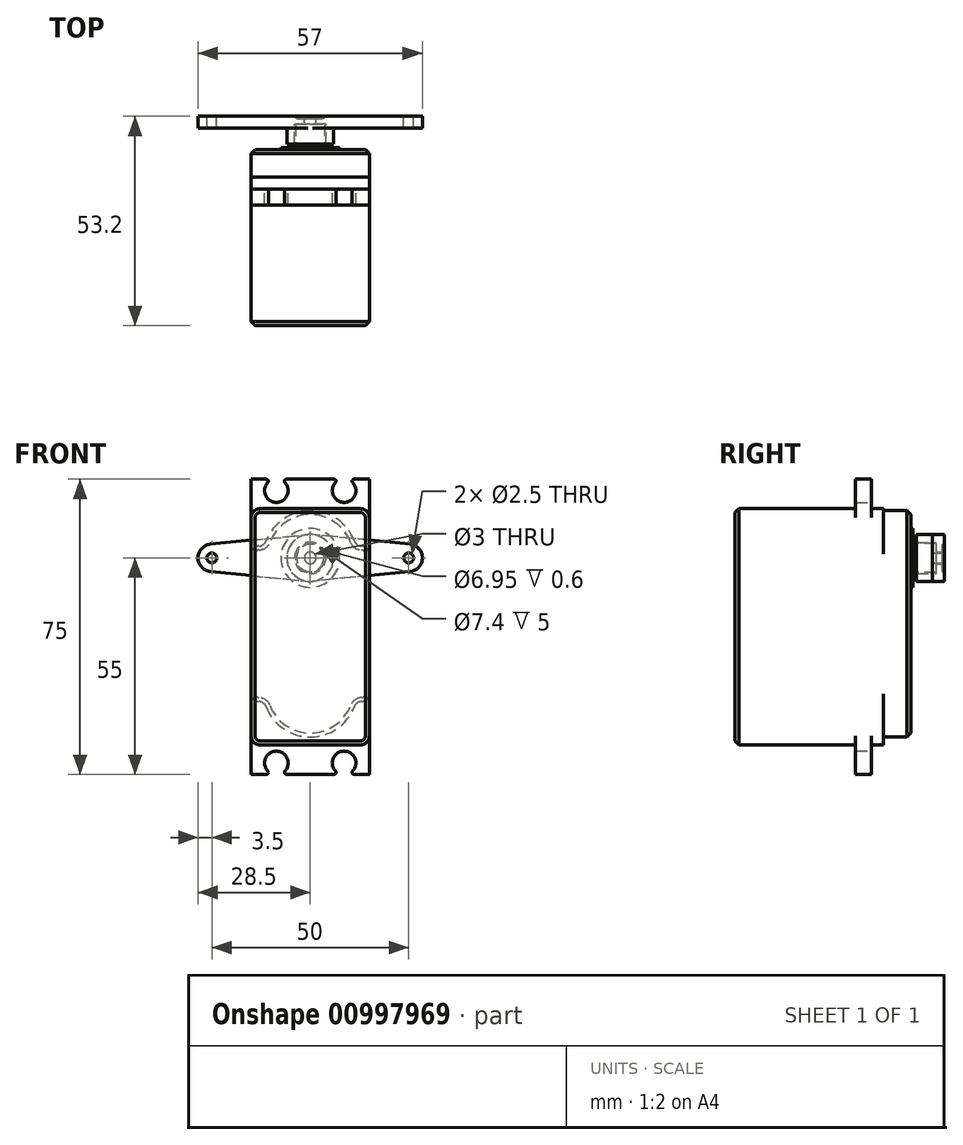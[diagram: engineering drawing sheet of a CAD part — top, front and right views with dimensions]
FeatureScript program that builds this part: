
annotation { "Feature Type Name" : "Feature", "Feature Type Description" : "" }
export const myFeature = defineFeature(function(context is Context, id is Id, definition is map)
    precondition{}
    {
        {
            var Q0;
            Q0=qCreatedBy(makeId("Front.planeOp"),FACE);
            var sketch = newSketch(context, id + "F0", { "sketchPlane" : qUnion([Q0])});
            skArc(sketch, "E0", {"start": v(-0.58, -5.92) * mm, "mid": v(0, -5.95) * mm, "end": v(0.58, -5.92) * mm});
            skCircle(sketch, "E1", {"center": v(0, 0) * mm, "radius": 28.5 * mm, "construction": true});
            skArc(sketch, "E2", {"start": v(-25.34, 3.48) * mm, "mid": v(-28.5, 0) * mm, "end": v(-25.34, -3.48) * mm});
            skArc(sketch, "E3.MirrorC", {"start": v(25.34, 3.48) * mm, "mid": v(28.5, 0) * mm, "end": v(25.34, -3.48) * mm});
            skLineSegment(sketch, "E4", {"start": v(-25.34, 3.48) * mm, "end": v(-0.58, 5.92) * mm});
            skLineSegment(sketch, "E5.MirrorCS", {"start": v(-25.34, -3.48) * mm, "end": v(-0.58, -5.92) * mm});
            skLineSegment(sketch, "E6.MirrorCS", {"start": v(25.34, 3.48) * mm, "end": v(0.58, 5.92) * mm});
            skLineSegment(sketch, "E7.MirrorCS", {"start": v(25.34, -3.48) * mm, "end": v(0.58, -5.92) * mm});
            skPoint(sketch, "E8.orphan", {"position": v(-30.14, 3.01) * mm});
            skPoint(sketch, "E9.orphan", {"position": v(-30.14, -3.01) * mm});
            skPoint(sketch, "E10.orphan", {"position": v(-3.18, 6.3) * mm});
            skPoint(sketch, "E11.orphan", {"position": v(3.18, 6.3) * mm});
            skPoint(sketch, "E12.orphan", {"position": v(-3.18, -6.3) * mm});
            skPoint(sketch, "E13.orphan", {"position": v(3.18, -6.3) * mm});
            skArc(sketch, "E14.trimOffspring", {"start": v(0.58, 5.92) * mm, "mid": v(0, 5.95) * mm, "end": v(-0.58, 5.92) * mm});
            skPoint(sketch, "E15.orphan", {"position": v(30.14, 3.01) * mm});
            skPoint(sketch, "E16.orphan", {"position": v(30.14, -3.01) * mm});
            skCircle(sketch, "E17", {"center": v(-25, 0) * mm, "radius": 1.25 * mm});
            skCircle(sketch, "E18.MirrorC", {"center": v(25, 0) * mm, "radius": 1.25 * mm});
            skSolve(sketch);
        }
        {
            var Q0;
            Q0=makeQuery(id+"F0.imprint","IMPRINT",FACE,{"disambiguationData":[TD([[makeQuery(id+"F0.imprint","IMPRINT",EDGE,{"derivedFrom":sQuery(id+"F0.wireOp",EDGE,"E0")}),1.0]])]});
            extrude(context, id + "F1", {"entities" : qUnion([Q0]), "depth" : 3 * mm, "offsetDistance" : 25 * mm});
        }
        {
            var Q0;
            Q0=makeQuery(id+"F1.opExtrude","CAP_FACE",FACE,{"disambiguationData":[OSD([sQuery(id+"F0.wireOp",EDGE,"E0"),sQuery(id+"F0.wireOp",EDGE,"E2"),sQuery(id+"F0.wireOp",EDGE,"E3.MirrorC"),sQuery(id+"F0.wireOp",EDGE,"E4"),sQuery(id+"F0.wireOp",EDGE,"E5.MirrorCS"),sQuery(id+"F0.wireOp",EDGE,"E6.MirrorCS"),sQuery(id+"F0.wireOp",EDGE,"E7.MirrorCS"),sQuery(id+"F0.wireOp",EDGE,"E14.trimOffspring"),sQuery(id+"F0.wireOp",EDGE,"E17"),sQuery(id+"F0.wireOp",EDGE,"E18.MirrorC")])],"isStart":false});
            var sketch = newSketch(context, id + "F2", { "sketchPlane" : qUnion([Q0])});
            skCircle(sketch, "E19", {"center": v(0, 0) * mm, "radius": 5.95 * mm});
            skSolve(sketch);
        }
        {
            var Q0;
            {var subQ0=sQuery(id+"F2.wireOp",EDGE,"E19");var subQ1=makeQuery(id+"F2.imprint","INTERSECT",VERTEX,{"derivedFrom":[makeQuery(id+"F1.opExtrude","CAP_EDGE",EDGE,{"disambiguationData":[OSD([sQuery(id+"F0.wireOp",EDGE,"E5.MirrorCS")])],"isStart":false}),subQ0]});Q0=makeQuery(id+"F2.imprint","IMPRINT",FACE,{"disambiguationData":[TD([[makeQuery(id+"F2.imprint","IMPRINT",EDGE,{"disambiguationData":[TD([[subQ1,-1.0]])],"derivedFrom":subQ0}),1.0]])]});}
            extrude(context, id + "F3", {"entities" : qUnion([Q0]), "operationType" : NewBodyOperationType.ADD, "depth" : 4 * mm, "offsetDistance" : 25 * mm});
        }
        {
            var Q0;
            Q0=makeQuery(id+"F1.opExtrude","CAP_FACE",FACE,{"disambiguationData":[OSD([sQuery(id+"F0.wireOp",EDGE,"E0"),sQuery(id+"F0.wireOp",EDGE,"E2"),sQuery(id+"F0.wireOp",EDGE,"E3.MirrorC"),sQuery(id+"F0.wireOp",EDGE,"E4"),sQuery(id+"F0.wireOp",EDGE,"E5.MirrorCS"),sQuery(id+"F0.wireOp",EDGE,"E6.MirrorCS"),sQuery(id+"F0.wireOp",EDGE,"E7.MirrorCS"),sQuery(id+"F0.wireOp",EDGE,"E14.trimOffspring"),sQuery(id+"F0.wireOp",EDGE,"E17"),sQuery(id+"F0.wireOp",EDGE,"E18.MirrorC")])],"isStart":true});
            var sketch = newSketch(context, id + "F4", { "sketchPlane" : qUnion([Q0])});
            skCircle(sketch, "E20", {"center": v(0, 0) * mm, "radius": 3.48 * mm});
            skSolve(sketch);
        }
        {
            var Q0;
            Q0=makeQuery(id+"F4.imprint","IMPRINT",FACE,{"disambiguationData":[TD([[makeQuery(id+"F4.imprint","IMPRINT",EDGE,{"derivedFrom":sQuery(id+"F4.wireOp",EDGE,"E20")}),1.0]])]});
            extrude(context, id + "F5", {"entities" : qUnion([Q0]), "operationType" : NewBodyOperationType.REMOVE, "oppositeDirection" : true, "depth" : 0.6 * mm, "offsetDistance" : 25 * mm});
        }
        {
            var Q0;
            Q0=makeQuery(id+"F5.boolean.opBoolean","COPY",FACE,{"derivedFrom":makeQuery(id+"F5.opExtrude","CAP_FACE",FACE,{"disambiguationData":[OSD([sQuery(id+"F4.wireOp",EDGE,"E20")])],"isStart":false})});
            var sketch = newSketch(context, id + "F6", { "sketchPlane" : qUnion([Q0])});
            skCircle(sketch, "E21", {"center": v(0, 0) * mm, "radius": 1.5 * mm});
            skSolve(sketch);
        }
        {
            var Q0;
            Q0=makeQuery(id+"F6.imprint","IMPRINT",FACE,{"disambiguationData":[TD([[makeQuery(id+"F6.imprint","IMPRINT",EDGE,{"derivedFrom":sQuery(id+"F6.wireOp",EDGE,"E21")}),1.0]])]});
            extrude(context, id + "F7", {"entities" : qUnion([Q0]), "operationType" : NewBodyOperationType.REMOVE, "oppositeDirection" : true, "depth" : 25 * mm, "offsetDistance" : 25 * mm});
        }
        {
            var Q0;
            Q0=makeQuery(id+"F3.opExtrude","CAP_FACE",FACE,{"disambiguationData":[OSD([sQuery(id+"F2.wireOp",EDGE,"E19")])],"isStart":false});
            var sketch = newSketch(context, id + "F8", { "sketchPlane" : qUnion([Q0])});
            skCircle(sketch, "E22", {"center": v(0, 0) * mm, "radius": 3.7 * mm});
            skSolve(sketch);
        }
        {
            var Q0;
            Q0 = qSketchRegion(id + "F8", true);
            extrude(context, id + "F9", {"entities" : qUnion([Q0]), "operationType" : NewBodyOperationType.REMOVE, "oppositeDirection" : true, "depth" : 5 * mm, "offsetDistance" : 25 * mm});
        }
        {
            var Q0;
            Q0=makeQuery(id+"F9.boolean.opBoolean","COPY",FACE,{"derivedFrom":makeQuery(id+"F9.opExtrude","CAP_FACE",FACE,{"disambiguationData":[OSD([sQuery(id+"F8.wireOp",EDGE,"E22")])],"isStart":false})});
            var sketch = newSketch(context, id + "F10", { "sketchPlane" : qUnion([Q0])});
            skCircle(sketch, "E23", {"center": v(0, 0) * mm, "radius": 3.98 * mm});
            skSolve(sketch);
        }
        {
            var Q0;
            Q0 = qSketchRegion(id + "F10", true);
            extrude(context, id + "F11", {"entities" : qUnion([Q0]), "depth" : 6 * mm, "offsetDistance" : 25 * mm});
        }
        {
            var Q0;
            Q0=makeQuery(id+"F11.opExtrude","CAP_FACE",FACE,{"disambiguationData":[OSD([sQuery(id+"F10.wireOp",EDGE,"E23")])],"isStart":false});
            var sketch = newSketch(context, id + "F12", { "sketchPlane" : qUnion([Q0])});
            skCircle(sketch, "E24", {"center": v(0, 0) * mm, "radius": 7.47 * mm});
            skSolve(sketch);
        }
        {
            var Q0;
            Q0 = qSketchRegion(id + "F12", true);
            extrude(context, id + "F13", {"entities" : qUnion([Q0]), "operationType" : NewBodyOperationType.ADD, "depth" : 0.5 * mm, "offsetDistance" : 25 * mm});
        }
        {
            var Q0;
            Q0=makeQuery(id+"F13.opExtrude","CAP_FACE",FACE,{"disambiguationData":[OSD([sQuery(id+"F12.wireOp",EDGE,"E24")])],"isStart":false});
            var sketch = newSketch(context, id + "F14", { "sketchPlane" : qUnion([Q0])});
            skLineSegment(sketch, "E25", {"start": v(0, 0) * mm, "end": v(0, 39.26) * mm, "construction": true});
            skLineSegment(sketch, "E26.left", {"start": v(-15, 3) * mm, "end": v(-15, -36.5) * mm});
            skLineSegment(sketch, "E26.right", {"start": v(15, 3) * mm, "end": v(15, -36.5) * mm});
            skArc(sketch, "E27", {"start": v(11.62, 3) * mm, "mid": v(0, 12) * mm, "end": v(-11.62, 3) * mm});
            skLineSegment(sketch, "E28", {"start": v(-15, 3) * mm, "end": v(-11.62, 3) * mm});
            skArc(sketch, "E29", {"start": v(-11.62, -36.5) * mm, "mid": v(0, -45.5) * mm, "end": v(11.62, -36.5) * mm});
            skLineSegment(sketch, "E30", {"start": v(-15, -36.5) * mm, "end": v(-11.62, -36.5) * mm});
            skLineSegment(sketch, "E31.trimOffspring", {"start": v(11.62, -36.5) * mm, "end": v(15, -36.5) * mm});
            skLineSegment(sketch, "E32.trimOffspring", {"start": v(11.62, 3) * mm, "end": v(15, 3) * mm});
            skSolve(sketch);
        }
        {
            var Q0;
            Q0 = qSketchRegion(id + "F14", true);
            extrude(context, id + "F15", {"entities" : qUnion([Q0]), "operationType" : NewBodyOperationType.ADD, "depth" : 7 * mm, "offsetDistance" : 25 * mm});
        }
        {
            var Q0;
            Q0=makeQuery(id+"F15.opExtrude","SWEPT_EDGE",EDGE,{"disambiguationData":[OSD([sQuery(id+"F14.wireOp",EDGE,"E27"),sQuery(id+"F14.wireOp",EDGE,"E28")])]});
            var Q1;
            Q1=makeQuery(id+"F15.opExtrude","SWEPT_EDGE",EDGE,{"disambiguationData":[OSD([sQuery(id+"F14.wireOp",EDGE,"E27"),sQuery(id+"F14.wireOp",EDGE,"E32.trimOffspring")])]});
            var Q2;
            Q2=makeQuery(id+"F15.opExtrude","SWEPT_EDGE",EDGE,{"disambiguationData":[OSD([sQuery(id+"F14.wireOp",EDGE,"E29"),sQuery(id+"F14.wireOp",EDGE,"E31.trimOffspring")])]});
            var Q3;
            Q3=makeQuery(id+"F15.opExtrude","SWEPT_EDGE",EDGE,{"disambiguationData":[OSD([sQuery(id+"F14.wireOp",EDGE,"E29"),sQuery(id+"F14.wireOp",EDGE,"E30")])]});
            fillet(context, id + "F16", {"entities" : qUnion([Q0, Q1, Q2, Q3]), "radius" : 2 * mm, "tangentPropagation" : true, "allowEdgeOverflow" : false});
        }
        {
            var Q0;
            Q0=makeQuery(id+"F15.opExtrude","SWEPT_EDGE",EDGE,{"disambiguationData":[OSD([sQuery(id+"F14.wireOp",EDGE,"E26.right"),sQuery(id+"F14.wireOp",EDGE,"E32.trimOffspring")])]});
            var Q1;
            Q1=makeQuery(id+"F15.opExtrude","SWEPT_EDGE",EDGE,{"disambiguationData":[OSD([sQuery(id+"F14.wireOp",EDGE,"E26.left"),sQuery(id+"F14.wireOp",EDGE,"E28")])]});
            var Q2;
            Q2=makeQuery(id+"F15.opExtrude","SWEPT_EDGE",EDGE,{"disambiguationData":[OSD([sQuery(id+"F14.wireOp",EDGE,"E26.right"),sQuery(id+"F14.wireOp",EDGE,"E31.trimOffspring")])]});
            var Q3;
            Q3=makeQuery(id+"F15.opExtrude","SWEPT_EDGE",EDGE,{"disambiguationData":[OSD([sQuery(id+"F14.wireOp",EDGE,"E26.left"),sQuery(id+"F14.wireOp",EDGE,"E30")])]});
            fillet(context, id + "F17", {"entities" : qUnion([Q0, Q1, Q2, Q3]), "radius" : 2 * mm, "tangentPropagation" : true, "allowEdgeOverflow" : false});
        }
        {
            var Q0;
            Q0=makeQuery(id+"F15.opExtrude","CAP_FACE",FACE,{"disambiguationData":[OSD([sQuery(id+"F14.wireOp",EDGE,"E26.left"),sQuery(id+"F14.wireOp",EDGE,"E26.right"),sQuery(id+"F14.wireOp",EDGE,"E27"),sQuery(id+"F14.wireOp",EDGE,"E28"),sQuery(id+"F14.wireOp",EDGE,"E29"),sQuery(id+"F14.wireOp",EDGE,"E30"),sQuery(id+"F14.wireOp",EDGE,"E31.trimOffspring"),sQuery(id+"F14.wireOp",EDGE,"E32.trimOffspring")])],"isStart":false});
            var sketch = newSketch(context, id + "F18", { "sketchPlane" : qUnion([Q0])});
            skPoint(sketch, "E33.firstSnap0", {"position": v(15, -33.9) * mm});
            skLineSegment(sketch, "E33.bottom", {"start": v(15, -47.5) * mm, "end": v(-15, -47.5) * mm});
            skLineSegment(sketch, "E33.top", {"start": v(15, 12.5) * mm, "end": v(-15, 12.5) * mm});
            skLineSegment(sketch, "E33.left", {"start": v(15, -47.5) * mm, "end": v(15, 12.5) * mm});
            skLineSegment(sketch, "E33.right", {"start": v(-15, -47.5) * mm, "end": v(-15, 12.5) * mm});
            skSolve(sketch);
        }
        {
            var Q0;
            Q0 = qSketchRegion(id + "F18", true);
            extrude(context, id + "F19", {"entities" : qUnion([Q0]), "operationType" : NewBodyOperationType.ADD, "depth" : 37.7 * mm, "offsetDistance" : 25 * mm});
        }
        {
            var Q0;
            {var subQ1=sQuery(id+"F14.wireOp",EDGE,"E27");var subQ5=sQuery(id+"F18.wireOp",EDGE,"E33.top");var subQ6=sQuery(id+"F18.wireOp",EDGE,"E33.left");var subQ7=sQuery(id+"F18.wireOp",EDGE,"E33.right");Q0=makeQuery(id+"F19.boolean.opBoolean","SPLIT",FACE,{"disambiguationData":[TD([makeQuery(id+"F15.opExtrude","SWEPT_FACE",FACE,{"disambiguationData":[OSD([subQ1])]})])],"derivedFrom":makeQuery(id+"F19.opExtrude","CAP_FACE",FACE,{"disambiguationData":[OSD([sQuery(id+"F18.wireOp",EDGE,"E33.bottom"),subQ5,subQ6,subQ7])],"isStart":true})});}
            cPlane(context, id + "F20", {"entities" : qUnion([Q0]), "cplaneType" : CPlaneType.OFFSET, "offset" : 3 * mm, "oppositeDirection" : true, "width" : 150 * mm, "height" : 150 * mm});
        }
        {
            var Q0;
            Q0=qCreatedBy(id+"F20.planeOp",FACE);
            var sketch = newSketch(context, id + "F21", { "sketchPlane" : qUnion([Q0])});
            skLineSegment(sketch, "E34.bottom", {"start": v(15, 20) * mm, "end": v(-15, 20) * mm});
            skLineSegment(sketch, "E34.top", {"start": v(15, -55) * mm, "end": v(-15, -55) * mm});
            skLineSegment(sketch, "E34.left", {"start": v(15, 20) * mm, "end": v(15, -55) * mm});
            skLineSegment(sketch, "E34.right", {"start": v(-15, 20) * mm, "end": v(-15, -55) * mm});
            skSolve(sketch);
        }
        {
            var Q0;
            Q0 = qSketchRegion(id + "F21", true);
            extrude(context, id + "F22", {"entities" : qUnion([Q0]), "operationType" : NewBodyOperationType.ADD, "oppositeDirection" : true, "depth" : 4 * mm, "offsetDistance" : 25 * mm});
        }
        {
            var Q0;
            {var subQ0=sQuery(id+"F18.wireOp",EDGE,"E33.left");var subQ1=sQuery(id+"F18.wireOp",EDGE,"E33.top");Q0=makeQuery(id+"F22.boolean.opBoolean","SPLIT",EDGE,{"disambiguationData":[TD([makeQuery(id+"F19.opExtrude","CAP_FACE",FACE,{"disambiguationData":[OSD([sQuery(id+"F18.wireOp",EDGE,"E33.bottom"),subQ1,subQ0,sQuery(id+"F18.wireOp",EDGE,"E33.right")])],"isStart":true})])],"derivedFrom":makeQuery(id+"F19.opExtrude","SWEPT_EDGE",EDGE,{"disambiguationData":[OSD([subQ1,subQ0])]})});}
            var Q1;
            {var subQ0=sQuery(id+"F18.wireOp",EDGE,"E33.right");var subQ1=sQuery(id+"F18.wireOp",EDGE,"E33.top");Q1=makeQuery(id+"F22.boolean.opBoolean","SPLIT",EDGE,{"disambiguationData":[TD([makeQuery(id+"F19.opExtrude","CAP_FACE",FACE,{"disambiguationData":[OSD([sQuery(id+"F18.wireOp",EDGE,"E33.bottom"),subQ1,sQuery(id+"F18.wireOp",EDGE,"E33.left"),subQ0])],"isStart":true})])],"derivedFrom":makeQuery(id+"F19.opExtrude","SWEPT_EDGE",EDGE,{"disambiguationData":[OSD([subQ1,subQ0])]})});}
            var Q2;
            {var subQ0=sQuery(id+"F18.wireOp",EDGE,"E33.left");var subQ1=sQuery(id+"F18.wireOp",EDGE,"E33.bottom");Q2=makeQuery(id+"F22.boolean.opBoolean","SPLIT",EDGE,{"disambiguationData":[TD([makeQuery(id+"F19.opExtrude","CAP_FACE",FACE,{"disambiguationData":[OSD([subQ1,sQuery(id+"F18.wireOp",EDGE,"E33.top"),subQ0,sQuery(id+"F18.wireOp",EDGE,"E33.right")])],"isStart":true})])],"derivedFrom":makeQuery(id+"F19.opExtrude","SWEPT_EDGE",EDGE,{"disambiguationData":[OSD([subQ1,subQ0])]})});}
            var Q3;
            {var subQ0=sQuery(id+"F18.wireOp",EDGE,"E33.right");var subQ1=sQuery(id+"F18.wireOp",EDGE,"E33.bottom");Q3=makeQuery(id+"F22.boolean.opBoolean","SPLIT",EDGE,{"disambiguationData":[TD([makeQuery(id+"F19.opExtrude","CAP_FACE",FACE,{"disambiguationData":[OSD([subQ1,sQuery(id+"F18.wireOp",EDGE,"E33.top"),sQuery(id+"F18.wireOp",EDGE,"E33.left"),subQ0])],"isStart":true})])],"derivedFrom":makeQuery(id+"F19.opExtrude","SWEPT_EDGE",EDGE,{"disambiguationData":[OSD([subQ1,subQ0])]})});}
            fillet(context, id + "F23", {"entities" : qUnion([Q0, Q1, Q2, Q3]), "radius" : (4.5 / 2) * mm, "tangentPropagation" : true, "allowEdgeOverflow" : false});
        }
        {
            var Q0;
            {var subQ0=sQuery(id+"F18.wireOp",EDGE,"E33.left");var subQ1=sQuery(id+"F18.wireOp",EDGE,"E33.top");Q0=makeQuery(id+"F22.boolean.opBoolean","SPLIT",EDGE,{"disambiguationData":[TD([makeQuery(id+"F19.opExtrude","CAP_FACE",FACE,{"disambiguationData":[OSD([sQuery(id+"F18.wireOp",EDGE,"E33.bottom"),subQ1,subQ0,sQuery(id+"F18.wireOp",EDGE,"E33.right")])],"isStart":false})])],"derivedFrom":makeQuery(id+"F19.opExtrude","SWEPT_EDGE",EDGE,{"disambiguationData":[OSD([subQ1,subQ0])]})});}
            var Q1;
            {var subQ0=sQuery(id+"F18.wireOp",EDGE,"E33.left");var subQ1=sQuery(id+"F18.wireOp",EDGE,"E33.bottom");Q1=makeQuery(id+"F22.boolean.opBoolean","SPLIT",EDGE,{"disambiguationData":[TD([makeQuery(id+"F19.opExtrude","CAP_FACE",FACE,{"disambiguationData":[OSD([subQ1,sQuery(id+"F18.wireOp",EDGE,"E33.top"),subQ0,sQuery(id+"F18.wireOp",EDGE,"E33.right")])],"isStart":false})])],"derivedFrom":makeQuery(id+"F19.opExtrude","SWEPT_EDGE",EDGE,{"disambiguationData":[OSD([subQ1,subQ0])]})});}
            var Q2;
            {var subQ0=sQuery(id+"F18.wireOp",EDGE,"E33.right");var subQ1=sQuery(id+"F18.wireOp",EDGE,"E33.bottom");Q2=makeQuery(id+"F22.boolean.opBoolean","SPLIT",EDGE,{"disambiguationData":[TD([makeQuery(id+"F19.opExtrude","CAP_FACE",FACE,{"disambiguationData":[OSD([subQ1,sQuery(id+"F18.wireOp",EDGE,"E33.top"),sQuery(id+"F18.wireOp",EDGE,"E33.left"),subQ0])],"isStart":false})])],"derivedFrom":makeQuery(id+"F19.opExtrude","SWEPT_EDGE",EDGE,{"disambiguationData":[OSD([subQ1,subQ0])]})});}
            var Q3;
            {var subQ0=sQuery(id+"F18.wireOp",EDGE,"E33.right");var subQ1=sQuery(id+"F18.wireOp",EDGE,"E33.top");Q3=makeQuery(id+"F22.boolean.opBoolean","SPLIT",EDGE,{"disambiguationData":[TD([makeQuery(id+"F19.opExtrude","CAP_FACE",FACE,{"disambiguationData":[OSD([sQuery(id+"F18.wireOp",EDGE,"E33.bottom"),subQ1,sQuery(id+"F18.wireOp",EDGE,"E33.left"),subQ0])],"isStart":false})])],"derivedFrom":makeQuery(id+"F19.opExtrude","SWEPT_EDGE",EDGE,{"disambiguationData":[OSD([subQ1,subQ0])]})});}
            fillet(context, id + "F24", {"entities" : qUnion([Q0, Q1, Q2, Q3]), "radius" : (4.5 / 2) * mm, "tangentPropagation" : true, "allowEdgeOverflow" : false});
        }
        {
            var Q0;
            Q0=makeQuery(id+"F19.opExtrude","CAP_FACE",FACE,{"disambiguationData":[OSD([sQuery(id+"F18.wireOp",EDGE,"E33.bottom"),sQuery(id+"F18.wireOp",EDGE,"E33.top"),sQuery(id+"F18.wireOp",EDGE,"E33.left"),sQuery(id+"F18.wireOp",EDGE,"E33.right")])],"isStart":false});
            chamfer(context, id + "F25", {"entities" : qUnion([Q0]), "width" : 1 * mm, "tangentPropagation" : true});
        }
        {
            var Q0;
            {var subQ0=sQuery(id+"F21.wireOp",EDGE,"E34.top");var subQ1=sQuery(id+"F21.wireOp",EDGE,"E34.left");var subQ2=sQuery(id+"F21.wireOp",EDGE,"E34.right");Q0=makeQuery(id+"F22.boolean.opBoolean","SPLIT",FACE,{"disambiguationData":[TD([makeQuery(id+"F19.opExtrude","SWEPT_FACE",FACE,{"disambiguationData":[OSD([sQuery(id+"F18.wireOp",EDGE,"E33.bottom")])]})])],"derivedFrom":makeQuery(id+"F22.opExtrude","CAP_FACE",FACE,{"disambiguationData":[OSD([sQuery(id+"F21.wireOp",EDGE,"E34.bottom"),subQ0,subQ1,subQ2])],"isStart":true})});}
            var sketch = newSketch(context, id + "F26", { "sketchPlane" : qUnion([Q0])});
            skCircle(sketch, "E35", {"center": v(-8.6, -52.1) * mm, "radius": 3 * mm});
            skLineSegment(sketch, "E36.0", {"start": v(15, -45.25) * mm, "end": v(15, 10.25) * mm, "construction": true});
            skLineSegment(sketch, "E37", {"start": v(15, -17.5) * mm, "end": v(-81.13, -17.5) * mm, "construction": true});
            skCircle(sketch, "E38.MirrorC", {"center": v(-8.6, 17.1) * mm, "radius": 3 * mm});
            skCircle(sketch, "E39.MirrorC", {"center": v(8.6, -52.1) * mm, "radius": 3 * mm});
            skCircle(sketch, "E40.MirrorC", {"center": v(8.6, 17.1) * mm, "radius": 3 * mm});
            skSolve(sketch);
        }
        {
            var Q0;
            Q0 = qSketchRegion(id + "F26", true);
            extrude(context, id + "F27", {"entities" : qUnion([Q0]), "operationType" : NewBodyOperationType.REMOVE, "oppositeDirection" : true, "depth" : 25 * mm, "offsetDistance" : 25 * mm});
        }
        {
            var Q0;
            Q0=makeQuery(id+"F27.boolean.opBoolean","INTERSECT",EDGE,{"disambiguationData":[OD(0.0)],"derivedFrom":[makeQuery(id+"F22.opExtrude","SWEPT_FACE",FACE,{"disambiguationData":[OSD([sQuery(id+"F21.wireOp",EDGE,"E34.top")])]}),makeQuery(id+"F27.opExtrude","SWEPT_FACE",FACE,{"disambiguationData":[OSD([sQuery(id+"F26.wireOp",EDGE,"E35")])]})]});
            var Q1;
            Q1=makeQuery(id+"F27.boolean.opBoolean","INTERSECT",EDGE,{"disambiguationData":[OD(1.0)],"derivedFrom":[makeQuery(id+"F22.opExtrude","SWEPT_FACE",FACE,{"disambiguationData":[OSD([sQuery(id+"F21.wireOp",EDGE,"E34.top")])]}),makeQuery(id+"F27.opExtrude","SWEPT_FACE",FACE,{"disambiguationData":[OSD([sQuery(id+"F26.wireOp",EDGE,"E35")])]})]});
            var Q2;
            Q2=makeQuery(id+"F27.boolean.opBoolean","INTERSECT",EDGE,{"disambiguationData":[OD(1.0)],"derivedFrom":[makeQuery(id+"F22.opExtrude","SWEPT_FACE",FACE,{"disambiguationData":[OSD([sQuery(id+"F21.wireOp",EDGE,"E34.top")])]}),makeQuery(id+"F27.opExtrude","SWEPT_FACE",FACE,{"disambiguationData":[OSD([sQuery(id+"F26.wireOp",EDGE,"E39.MirrorC")])]})]});
            var Q3;
            Q3=makeQuery(id+"F27.boolean.opBoolean","INTERSECT",EDGE,{"disambiguationData":[OD(0.0)],"derivedFrom":[makeQuery(id+"F22.opExtrude","SWEPT_FACE",FACE,{"disambiguationData":[OSD([sQuery(id+"F21.wireOp",EDGE,"E34.top")])]}),makeQuery(id+"F27.opExtrude","SWEPT_FACE",FACE,{"disambiguationData":[OSD([sQuery(id+"F26.wireOp",EDGE,"E39.MirrorC")])]})]});
            var Q4;
            Q4=makeQuery(id+"F27.boolean.opBoolean","INTERSECT",EDGE,{"disambiguationData":[OD(0.0)],"derivedFrom":[makeQuery(id+"F22.opExtrude","SWEPT_FACE",FACE,{"disambiguationData":[OSD([sQuery(id+"F21.wireOp",EDGE,"E34.bottom")])]}),makeQuery(id+"F27.opExtrude","SWEPT_FACE",FACE,{"disambiguationData":[OSD([sQuery(id+"F26.wireOp",EDGE,"E38.MirrorC")])]})]});
            var Q5;
            Q5=makeQuery(id+"F27.boolean.opBoolean","INTERSECT",EDGE,{"disambiguationData":[OD(1.0)],"derivedFrom":[makeQuery(id+"F22.opExtrude","SWEPT_FACE",FACE,{"disambiguationData":[OSD([sQuery(id+"F21.wireOp",EDGE,"E34.bottom")])]}),makeQuery(id+"F27.opExtrude","SWEPT_FACE",FACE,{"disambiguationData":[OSD([sQuery(id+"F26.wireOp",EDGE,"E38.MirrorC")])]})]});
            var Q6;
            Q6=makeQuery(id+"F27.boolean.opBoolean","INTERSECT",EDGE,{"disambiguationData":[OD(1.0)],"derivedFrom":[makeQuery(id+"F22.opExtrude","SWEPT_FACE",FACE,{"disambiguationData":[OSD([sQuery(id+"F21.wireOp",EDGE,"E34.bottom")])]}),makeQuery(id+"F27.opExtrude","SWEPT_FACE",FACE,{"disambiguationData":[OSD([sQuery(id+"F26.wireOp",EDGE,"E40.MirrorC")])]})]});
            var Q7;
            Q7=makeQuery(id+"F27.boolean.opBoolean","INTERSECT",EDGE,{"disambiguationData":[OD(0.0)],"derivedFrom":[makeQuery(id+"F22.opExtrude","SWEPT_FACE",FACE,{"disambiguationData":[OSD([sQuery(id+"F21.wireOp",EDGE,"E34.bottom")])]}),makeQuery(id+"F27.opExtrude","SWEPT_FACE",FACE,{"disambiguationData":[OSD([sQuery(id+"F26.wireOp",EDGE,"E40.MirrorC")])]})]});
            fillet(context, id + "F28", {"entities" : qUnion([Q0, Q1, Q2, Q3, Q4, Q5, Q6, Q7]), "radius" : 0.5 * mm, "tangentPropagation" : true, "allowEdgeOverflow" : false});
        }
        {
            var Q0;
            Q0=makeQuery(id+"F15.opExtrude","CAP_EDGE",EDGE,{"disambiguationData":[OSD([sQuery(id+"F14.wireOp",EDGE,"E26.left")])],"isStart":true});
            chamfer(context, id + "F29", {"entities" : qUnion([Q0]), "width" : 1 * mm, "tangentPropagation" : true});
        }
    });
